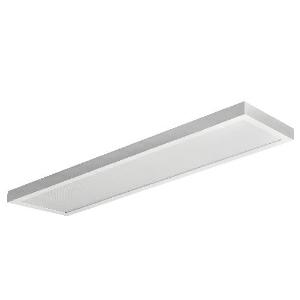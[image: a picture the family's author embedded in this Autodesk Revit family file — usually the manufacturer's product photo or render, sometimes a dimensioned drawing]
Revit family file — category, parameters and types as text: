
# Revit family: ledpanels-sf-p_l15-50w-dali-830_840_542003156300_3deb
name_source: partatom
category: Lighting Fixtures
units: mm (PartAtom-declared; Revit-internal decimal feet)

## family parameters
Cut with Voids When Loaded = No
Host = Face
Light Source = No
Part Type = Normal
Room Calculation Point = No
Round Connector Dimension = Use Diameter
Shared = No

## types (1)
- LEDPanelS-Sf-P L15-50W-DALI-830/840 (1 x LED, 6250 lm, 4000)
    Apparent Load = 50 VA
    Approval mark = CE, ENEC
    CIE Flux Codes = 60 87 97 100 100
    Color Rendering = 80
    Color Temperature = 4000
    Control Gear = Electronic ballast
    Default Elevation = 1800 mm
    Description = Panel Performer Surface Mounted 1574x370mm-50W-6250lm-3/4000K-DALI
    Frequency = 60 Hz
    Height = 55 mm
    Lamp = 1 x LED
    Lamp Light Flux = 6250 lm
    Lamp count = 1
    Length = 1574 mm
    Luminous efficacy = 125 lm/W
    Manufacturer = OPPLE
    ModVariant = No
    Model = 542003156300
    Mounting Place = Ceiling
    Mounting Type = Surface mounted
    Number of Poles = 1
    OnlyDefault = Yes
    Power Factor = 1
    Product Name = LEDPanelS-Sf-P L15-50W-DALI-830/840
    Product group = Ceiling mounted luminaire
    ProductGroupID = 3
    Protection Class = Protection class II
    Protection Degree = IP 20
    RLX_Detail_Level = 1
    RLX_Emergency_Light_Flux = 0 lm
    RLX_Emergency_Type = 0
    RLX_Emergency_Type_DB = No
    RlxData = <blob elided: 100093 chars, md5=f10f003b>
    Socket = socket
    Standby Power = 0 W
    System Light Flux = 6250 lm
    System Power = 50 W
    Type Comments = Product without accessories
    Type Image = web_surface_pl.jpg
    URL = http://relux.com
    VarID = ---
    Voltage = 230 V
    Voltage Range = 220-240 V
    Weight = 0.00 kg
    Width = 370 mm

## geometry (parser evidence)
native form markers: Blend x4, Sweep x10
no freeform markers — native parametric forms only
